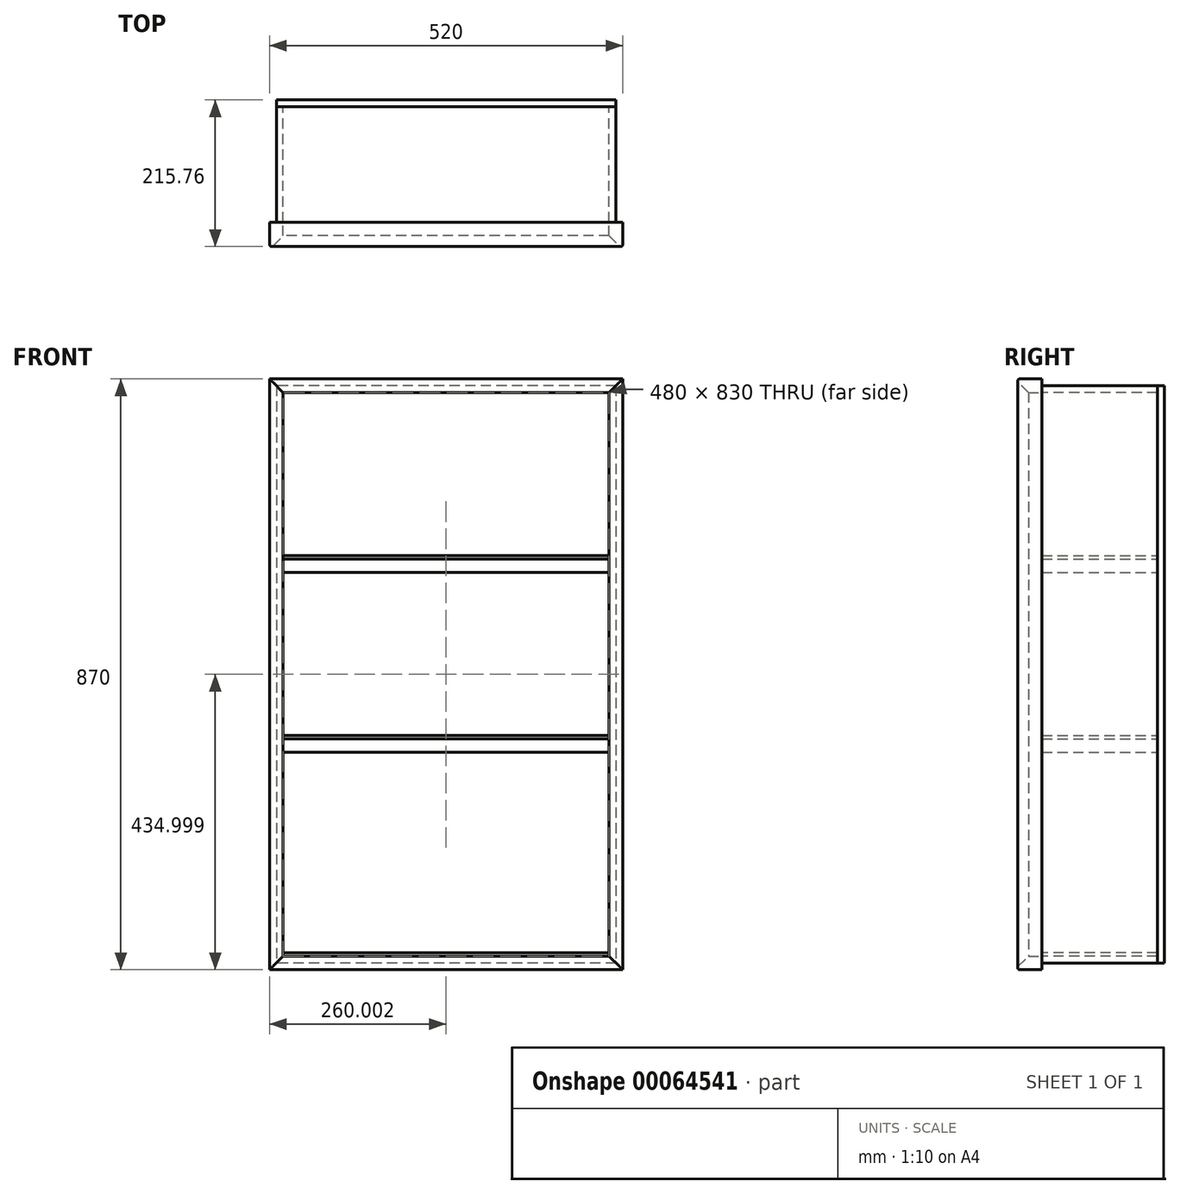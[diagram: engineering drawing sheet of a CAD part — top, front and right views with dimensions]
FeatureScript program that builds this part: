
annotation { "Feature Type Name" : "Feature", "Feature Type Description" : "" }
export const myFeature = defineFeature(function(context is Context, id is Id, definition is map)
    precondition{}
    {
        {
            var Q0;
            Q0=qCreatedBy(makeId("Front.planeOp"),FACE);
            var sketch = newSketch(context, id + "F0", { "sketchPlane" : qUnion([Q0])});
            skLineSegment(sketch, "E0.bottom", {"start": v(-62.83, 773.37) * mm, "end": v(457.17, 773.37) * mm});
            skLineSegment(sketch, "E0.top", {"start": v(-62.83, -96.63) * mm, "end": v(457.17, -96.63) * mm});
            skLineSegment(sketch, "E0.left", {"start": v(-62.83, 773.37) * mm, "end": v(-62.83, -96.63) * mm});
            skLineSegment(sketch, "E0.right", {"start": v(457.17, 773.37) * mm, "end": v(457.17, -96.63) * mm});
            skLineSegment(sketch, "E1.bottom", {"start": v(-42.83, 753.37) * mm, "end": v(437.17, 753.37) * mm});
            skLineSegment(sketch, "E1.top", {"start": v(-42.83, -76.63) * mm, "end": v(437.17, -76.63) * mm});
            skLineSegment(sketch, "E1.left", {"start": v(-42.83, 753.37) * mm, "end": v(-42.83, -76.63) * mm});
            skLineSegment(sketch, "E1.right", {"start": v(437.17, 753.37) * mm, "end": v(437.17, -76.63) * mm});
            skSolve(sketch);
        }
        {
            var Q0;
            Q0=makeQuery(id+"F0.imprint","IMPRINT",FACE,{"disambiguationData":[TD([[makeQuery(id+"F0.imprint","IMPRINT",EDGE,{"derivedFrom":sQuery(id+"F0.wireOp",EDGE,"E0.bottom")}),-1.0]])]});
            extrude(context, id + "F1", {"entities" : qUnion([Q0]), "depth" : 40 * mm});
        }
        {
            var Q0;
            Q0=makeQuery(id+"F1.opExtrude","CAP_EDGE",EDGE,{"disambiguationData":[OSD([sQuery(id+"F0.wireOp",EDGE,"E1.right")])],"isStart":false});
            var Q1;
            Q1=makeQuery(id+"F1.opExtrude","CAP_EDGE",EDGE,{"disambiguationData":[OSD([sQuery(id+"F0.wireOp",EDGE,"E1.bottom")])],"isStart":false});
            var Q2;
            Q2=makeQuery(id+"F1.opExtrude","CAP_EDGE",EDGE,{"disambiguationData":[OSD([sQuery(id+"F0.wireOp",EDGE,"E1.left")])],"isStart":false});
            var Q3;
            Q3=makeQuery(id+"F1.opExtrude","CAP_EDGE",EDGE,{"disambiguationData":[OSD([sQuery(id+"F0.wireOp",EDGE,"E1.top")])],"isStart":false});
            chamfer(context, id + "F2", {"entities" : qUnion([Q0, Q1, Q2, Q3]), "width" : 20 * mm, "tangentPropagation" : true});
        }
        {
            var Q0;
            Q0=makeQuery(id+"F2.opChamfer","BLEND_EDGE",EDGE,{"blendedFrom":[makeQuery(id+"F1.opExtrude","CAP_EDGE",EDGE,{"disambiguationData":[OSD([sQuery(id+"F0.wireOp",EDGE,"E1.left")])],"isStart":false}),makeQuery(id+"F1.opExtrude","SWEPT_FACE",FACE,{"disambiguationData":[OSD([sQuery(id+"F0.wireOp",EDGE,"E0.left")])]})],"blendedInto":[makeQuery(id+"F1.opExtrude","SWEPT_FACE",FACE,{"disambiguationData":[OSD([sQuery(id+"F0.wireOp",EDGE,"E0.left")])]})]});
            var Q1;
            Q1=makeQuery(id+"F2.opChamfer","BLEND_EDGE",EDGE,{"blendedFrom":[makeQuery(id+"F1.opExtrude","CAP_EDGE",EDGE,{"disambiguationData":[OSD([sQuery(id+"F0.wireOp",EDGE,"E1.right")])],"isStart":false}),makeQuery(id+"F1.opExtrude","SWEPT_FACE",FACE,{"disambiguationData":[OSD([sQuery(id+"F0.wireOp",EDGE,"E0.right")])]})],"blendedInto":[makeQuery(id+"F1.opExtrude","SWEPT_FACE",FACE,{"disambiguationData":[OSD([sQuery(id+"F0.wireOp",EDGE,"E0.right")])]})]});
            var Q2;
            Q2=makeQuery(id+"F2.opChamfer","BLEND_EDGE",EDGE,{"blendedFrom":[makeQuery(id+"F1.opExtrude","CAP_EDGE",EDGE,{"disambiguationData":[OSD([sQuery(id+"F0.wireOp",EDGE,"E1.bottom")])],"isStart":false}),makeQuery(id+"F1.opExtrude","SWEPT_FACE",FACE,{"disambiguationData":[OSD([sQuery(id+"F0.wireOp",EDGE,"E0.bottom")])]})],"blendedInto":[makeQuery(id+"F1.opExtrude","SWEPT_FACE",FACE,{"disambiguationData":[OSD([sQuery(id+"F0.wireOp",EDGE,"E0.bottom")])]})]});
            var Q3;
            Q3=makeQuery(id+"F2.opChamfer","BLEND_EDGE",EDGE,{"blendedFrom":[makeQuery(id+"F1.opExtrude","CAP_EDGE",EDGE,{"disambiguationData":[OSD([sQuery(id+"F0.wireOp",EDGE,"E1.top")])],"isStart":false}),makeQuery(id+"F1.opExtrude","SWEPT_FACE",FACE,{"disambiguationData":[OSD([sQuery(id+"F0.wireOp",EDGE,"E0.top")])]})],"blendedInto":[makeQuery(id+"F1.opExtrude","SWEPT_FACE",FACE,{"disambiguationData":[OSD([sQuery(id+"F0.wireOp",EDGE,"E0.top")])]})]});
            fillet(context, id + "F3", {"entities" : qUnion([Q0, Q1, Q2, Q3]), "radius" : 3 * mm, "tangentPropagation" : true, "allowEdgeOverflow" : false});
        }
        {
            var Q0;
            Q0=makeQuery(id+"F1.opExtrude","CAP_FACE",FACE,{"disambiguationData":[OSD([sQuery(id+"F0.wireOp",EDGE,"E0.bottom"),sQuery(id+"F0.wireOp",EDGE,"E0.top"),sQuery(id+"F0.wireOp",EDGE,"E0.left"),sQuery(id+"F0.wireOp",EDGE,"E0.right"),sQuery(id+"F0.wireOp",EDGE,"E1.bottom"),sQuery(id+"F0.wireOp",EDGE,"E1.top"),sQuery(id+"F0.wireOp",EDGE,"E1.left"),sQuery(id+"F0.wireOp",EDGE,"E1.right")])],"isStart":true});
            var sketch = newSketch(context, id + "F4", { "sketchPlane" : qUnion([Q0])});
            skLineSegment(sketch, "E2.bottom", {"start": v(-432.17, 748.37) * mm, "end": v(37.83, 748.37) * mm});
            skLineSegment(sketch, "E2.top", {"start": v(-432.17, -71.63) * mm, "end": v(37.83, -71.63) * mm});
            skLineSegment(sketch, "E2.left", {"start": v(-432.17, 748.37) * mm, "end": v(-432.17, -71.63) * mm});
            skLineSegment(sketch, "E2.right", {"start": v(37.83, 748.37) * mm, "end": v(37.83, -71.63) * mm});
            skSolve(sketch);
        }
        {
            var Q0;
            Q0=makeQuery(id+"F4.imprint","IMPRINT",FACE,{"disambiguationData":[TD([[makeQuery(id+"F4.imprint","IMPRINT",EDGE,{"derivedFrom":makeQuery(id+"F1.opExtrude","CAP_EDGE",EDGE,{"disambiguationData":[OSD([sQuery(id+"F0.wireOp",EDGE,"E0.bottom")])],"isStart":true})}),1.0]])]});
            var sketch = newSketch(context, id + "F5", { "sketchPlane" : qUnion([Q0])});
            skLineSegment(sketch, "E3.bottom", {"start": v(-447.17, 763.37) * mm, "end": v(52.83, 763.37) * mm});
            skLineSegment(sketch, "E3.top", {"start": v(-447.17, -86.63) * mm, "end": v(52.83, -86.63) * mm});
            skLineSegment(sketch, "E3.left", {"start": v(-447.17, 763.37) * mm, "end": v(-447.17, -86.63) * mm});
            skLineSegment(sketch, "E3.right", {"start": v(52.83, 763.37) * mm, "end": v(52.83, -86.63) * mm});
            skLineSegment(sketch, "E4.bottom", {"start": v(-437.17, 753.37) * mm, "end": v(42.83, 753.37) * mm});
            skLineSegment(sketch, "E4.top", {"start": v(-437.17, -76.63) * mm, "end": v(42.83, -76.63) * mm});
            skLineSegment(sketch, "E4.left", {"start": v(-437.17, 753.37) * mm, "end": v(-437.17, -76.63) * mm});
            skLineSegment(sketch, "E4.right", {"start": v(42.83, 753.37) * mm, "end": v(42.83, -76.63) * mm});
            skSolve(sketch);
        }
        {
            var Q0;
            Q0=makeQuery(id+"F5.imprint","IMPRINT",FACE,{"disambiguationData":[TD([[makeQuery(id+"F5.imprint","IMPRINT",EDGE,{"derivedFrom":sQuery(id+"F5.wireOp",EDGE,"E3.bottom")}),-1.0]])]});
            extrude(context, id + "F6", {"entities" : qUnion([Q0]), "depth" : 170 * mm});
        }
        {
            var Q0;
            Q0=makeQuery(id+"F6.opExtrude","CAP_FACE",FACE,{"disambiguationData":[OSD([sQuery(id+"F5.wireOp",EDGE,"E3.bottom"),sQuery(id+"F5.wireOp",EDGE,"E3.top"),sQuery(id+"F5.wireOp",EDGE,"E3.left"),sQuery(id+"F5.wireOp",EDGE,"E3.right"),sQuery(id+"F5.wireOp",EDGE,"E4.bottom"),sQuery(id+"F5.wireOp",EDGE,"E4.top"),sQuery(id+"F5.wireOp",EDGE,"E4.left"),sQuery(id+"F5.wireOp",EDGE,"E4.right")])],"isStart":false});
            var sketch = newSketch(context, id + "F7", { "sketchPlane" : qUnion([Q0])});
            skLineSegment(sketch, "E5.bottom", {"start": v(-447.17, 763.37) * mm, "end": v(52.83, 763.37) * mm});
            skLineSegment(sketch, "E5.top", {"start": v(-447.17, -86.63) * mm, "end": v(52.83, -86.63) * mm});
            skLineSegment(sketch, "E5.left", {"start": v(-447.17, 763.37) * mm, "end": v(-447.17, -86.63) * mm});
            skLineSegment(sketch, "E5.right", {"start": v(52.83, 763.37) * mm, "end": v(52.83, -86.63) * mm});
            skSolve(sketch);
        }
        {
            var Q0;
            Q0=makeQuery(id+"F7.imprint","IMPRINT",FACE,{"disambiguationData":[TD([[makeQuery(id+"F7.imprint","IMPRINT",EDGE,{"derivedFrom":makeQuery(id+"F6.opExtrude","CAP_EDGE",EDGE,{"disambiguationData":[OSD([sQuery(id+"F5.wireOp",EDGE,"E4.bottom")])],"isStart":false})}),1.0]])]});
            var Q1;
            Q1=makeQuery(id+"F7.imprint","IMPRINT",FACE,{"disambiguationData":[TD([[makeQuery(id+"F7.imprint","IMPRINT",EDGE,{"derivedFrom":sQuery(id+"F7.wireOp",EDGE,"E5.bottom")}),-1.0]])]});
            extrude(context, id + "F8", {"entities" : qUnion([Q0, Q1]), "depth" : 10 * mm});
        }
        {
            var Q0;
            Q0=makeQuery(id+"F8.opExtrude","CAP_FACE",FACE,{"disambiguationData":[OSD([sQuery(id+"F7.wireOp",EDGE,"E5.bottom"),sQuery(id+"F7.wireOp",EDGE,"E5.top"),sQuery(id+"F7.wireOp",EDGE,"E5.left"),sQuery(id+"F7.wireOp",EDGE,"E5.right")])],"isStart":true});
            var sketch = newSketch(context, id + "F9", { "sketchPlane" : qUnion([Q0])});
            skLineSegment(sketch, "E6.bottom", {"start": v(437.17, 508.37) * mm, "end": v(-42.83, 508.37) * mm});
            skLineSegment(sketch, "E6.top", {"start": v(437.17, 488.37) * mm, "end": v(-42.83, 488.37) * mm});
            skLineSegment(sketch, "E6.left", {"start": v(437.17, 508.37) * mm, "end": v(437.17, 488.37) * mm});
            skLineSegment(sketch, "E6.right", {"start": v(-42.83, 508.37) * mm, "end": v(-42.83, 488.37) * mm});
            skLineSegment(sketch, "E7.bottom", {"start": v(437.17, 243.37) * mm, "end": v(-42.83, 243.37) * mm});
            skLineSegment(sketch, "E7.top", {"start": v(437.17, 223.37) * mm, "end": v(-42.83, 223.37) * mm});
            skLineSegment(sketch, "E7.left", {"start": v(437.17, 243.37) * mm, "end": v(437.17, 223.37) * mm});
            skLineSegment(sketch, "E7.right", {"start": v(-42.83, 243.37) * mm, "end": v(-42.83, 223.37) * mm});
            skSolve(sketch);
        }
        {
            var Q0;
            Q0=makeQuery(id+"F9.imprint","IMPRINT",FACE,{"disambiguationData":[TD([[makeQuery(id+"F9.imprint","IMPRINT",EDGE,{"derivedFrom":sQuery(id+"F9.wireOp",EDGE,"E6.bottom")}),1.0]])]});
            var Q1;
            Q1=makeQuery(id+"F9.imprint","IMPRINT",FACE,{"disambiguationData":[TD([[makeQuery(id+"F9.imprint","IMPRINT",EDGE,{"derivedFrom":sQuery(id+"F9.wireOp",EDGE,"E7.bottom")}),1.0]])]});
            extrude(context, id + "F10", {"entities" : qUnion([Q0, Q1]), "depth" : 170 * mm});
        }
        {
            var Q0;
            Q0=makeQuery(id+"F10.opExtrude","SWEPT_FACE",FACE,{"disambiguationData":[OSD([sQuery(id+"F9.wireOp",EDGE,"E6.bottom")])]});
            extrude(context, id + "F11", {"entities" : qUnion([Q0]), "depth" : 5 * mm});
        }
        {
            var Q0;
            Q0=makeQuery(id+"F10.opExtrude","SWEPT_FACE",FACE,{"disambiguationData":[OSD([sQuery(id+"F9.wireOp",EDGE,"E7.bottom")])]});
            extrude(context, id + "F12", {"entities" : qUnion([Q0]), "depth" : 5 * mm});
        }
        {
            var Q0;
            Q0=makeQuery(id+"F6.opExtrude","SWEPT_FACE",FACE,{"disambiguationData":[OSD([sQuery(id+"F5.wireOp",EDGE,"E4.top")])]});
            extrude(context, id + "F13", {"entities" : qUnion([Q0]), "depth" : 5 * mm});
        }
    });
